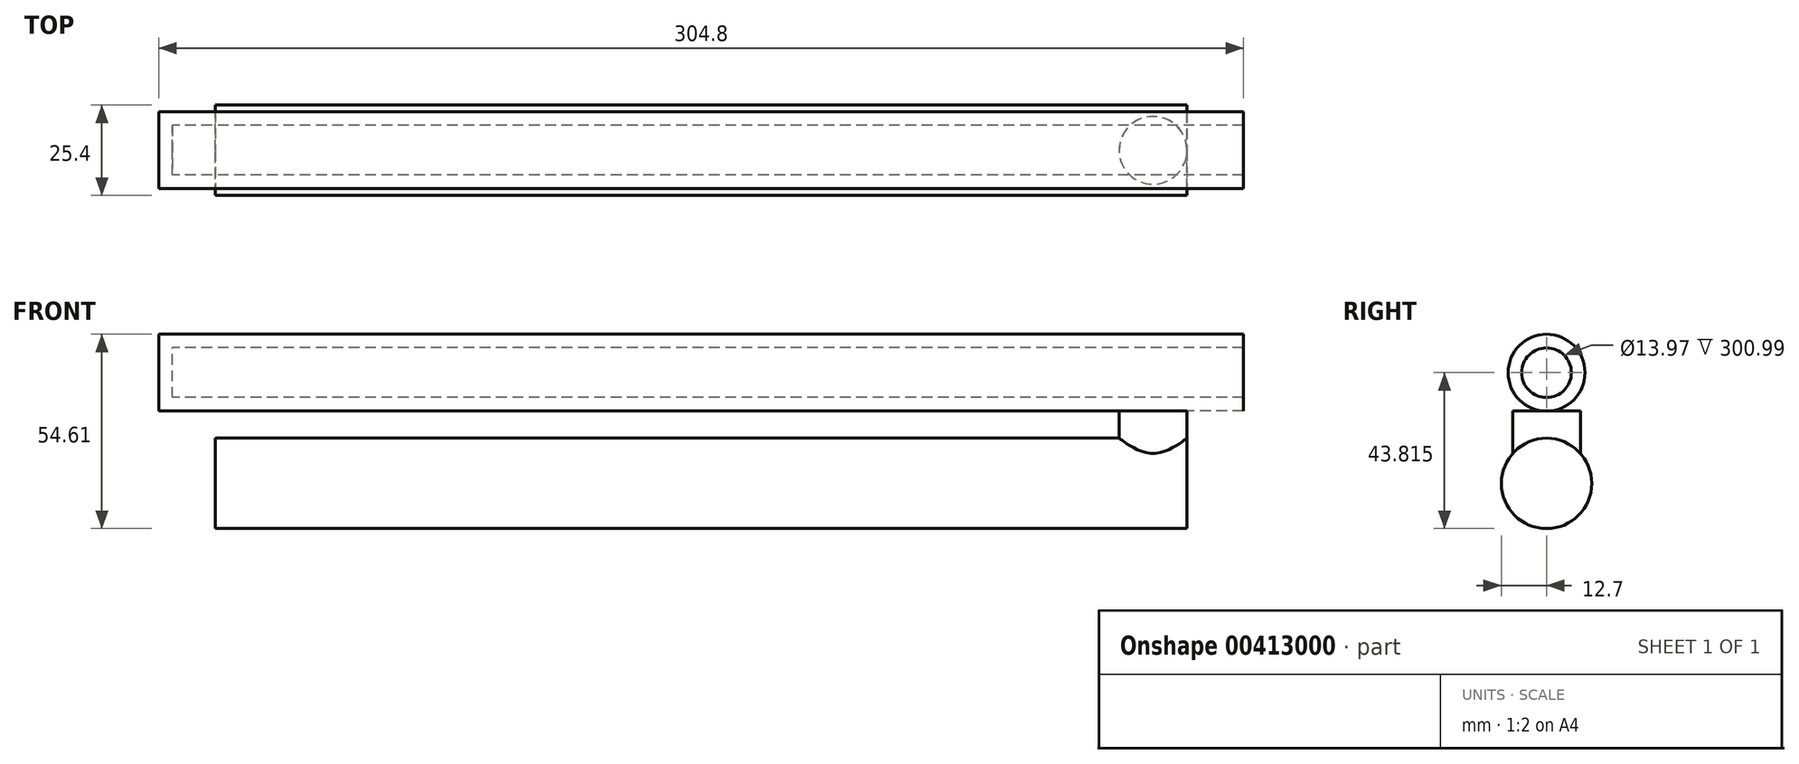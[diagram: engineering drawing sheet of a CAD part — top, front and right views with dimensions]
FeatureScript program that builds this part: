
annotation { "Feature Type Name" : "Feature", "Feature Type Description" : "" }
export const myFeature = defineFeature(function(context is Context, id is Id, definition is map)
    precondition{}
    {
        {
            var Q0;
            Q0=qCreatedBy(makeId("Right.planeOp"),FACE);
            var sketch = newSketch(context, id + "F0", { "sketchPlane" : qUnion([Q0])});
            skCircle(sketch, "E0", {"center": v(0, 0) * mm, "radius": 12.7 * mm});
            skSolve(sketch);
        }
        {
            var Q0;
            Q0=makeQuery(id+"F0.imprint","IMPRINT",FACE,{"disambiguationData":[TD([[makeQuery(id+"F0.imprint","IMPRINT",EDGE,{"derivedFrom":sQuery(id+"F0.wireOp",EDGE,"E0")}),1.0]])]});
            extrude(context, id + "F1", {"entities" : qUnion([Q0]), "endBound" : BoundingType.SYMMETRIC, "depth" : 273.05 * mm});
        }
        {
            var Q0;
            Q0=qCreatedBy(makeId("Top.planeOp"),FACE);
            var sketch = newSketch(context, id + "F2", { "sketchPlane" : qUnion([Q0])});
            skLineSegment(sketch, "E1.0", {"start": v(136.53, 12.7) * mm, "end": v(136.53, -12.7) * mm, "construction": true});
            skCircle(sketch, "E2", {"center": v(127, 0) * mm, "radius": 9.53 * mm});
            skSolve(sketch);
        }
        {
            var Q0;
            Q0 = qSketchRegion(id + "F2", true);
            extrude(context, id + "F3", {"entities" : qUnion([Q0]), "operationType" : NewBodyOperationType.ADD, "depth" : 20.32 * mm});
        }
        {
            var Q0;
            Q0=qCreatedBy(makeId("Right.planeOp"),FACE);
            var sketch = newSketch(context, id + "F4", { "sketchPlane" : qUnion([Q0])});
            skCircle(sketch, "E3", {"center": v(0, 31.12) * mm, "radius": 10.8 * mm});
            skSolve(sketch);
        }
        {
            var Q0;
            Q0=makeQuery(id+"F4.imprint","IMPRINT",FACE,{"disambiguationData":[TD([[makeQuery(id+"F4.imprint","IMPRINT",EDGE,{"derivedFrom":sQuery(id+"F4.wireOp",EDGE,"E3")}),1.0]])]});
            extrude(context, id + "F5", {"entities" : qUnion([Q0]), "endBound" : BoundingType.SYMMETRIC, "depth" : 304.8 * mm});
        }
        {
            var Q0;
            Q0=makeQuery(id+"F5.opExtrude","CAP_FACE",FACE,{"disambiguationData":[OSD([sQuery(id+"F4.wireOp",EDGE,"E3")])],"isStart":false});
            shell(context, id + "F6", {"entities" : qUnion([Q0]), "thickness" : 3.8 * mm});
        }
    });
